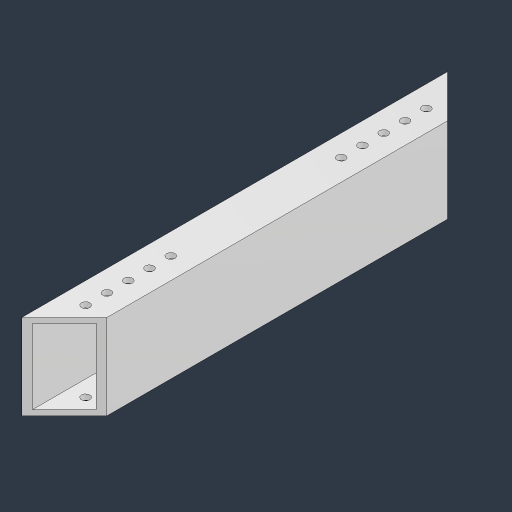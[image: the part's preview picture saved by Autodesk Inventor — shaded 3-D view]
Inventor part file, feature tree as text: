
AUTODESK INVENTOR PART (.ipt)
format: ipt  version: 2024.3 (Build 283343000, 343)  size: 145,920 bytes
history: native  units: in
note: dims shown in document units (in); Inventor stores cm internally (conversion verified against a paired STEP export)
features: sketch x3, extrude x2, hole x1, mirror x1, projected_geometry x1
ambient origin geometry x8: Origin, YZ Plane, XZ Plane, XY Plane, X Axis, Y Axis, Z Axis, Center Point
bodies: Solid1 (feature_tree)
feature tree (8):
  extrude  "Extrusion1"  Depth=2.0in
  extrude  "Extrusion2"  Depth=0.125in TaperAngle=0.0deg
  hole  "Hole1"  [1 undecoded]
  mirror  "Mirror1"
  sketch  "Sketch1"  dims[d0=1.0in d1=2.0in]
  sketch  "Sketch2"  dims[d2=0.125in d3=10.0in d4=0.0in]
  projected_geometry  "Projected Loop1"
  sketch  "Sketch4"  dims[d6=45.0deg d7=0.0in d8=0.0in d9=0.5in d10=1.0in d11=1.9685in d13=0.5in d14=0.3937in d16=1.0in d18=0.201in d19=0.38in d20=0.375in d21=0.25in d22=0.5635in d23=1.0in d24=0.8108in]
note: 1 required parameter value undecoded (feature->parameter linkage not recoverable at this tier; creation-order binding heuristic only, values carry confidence <= 0.55)
